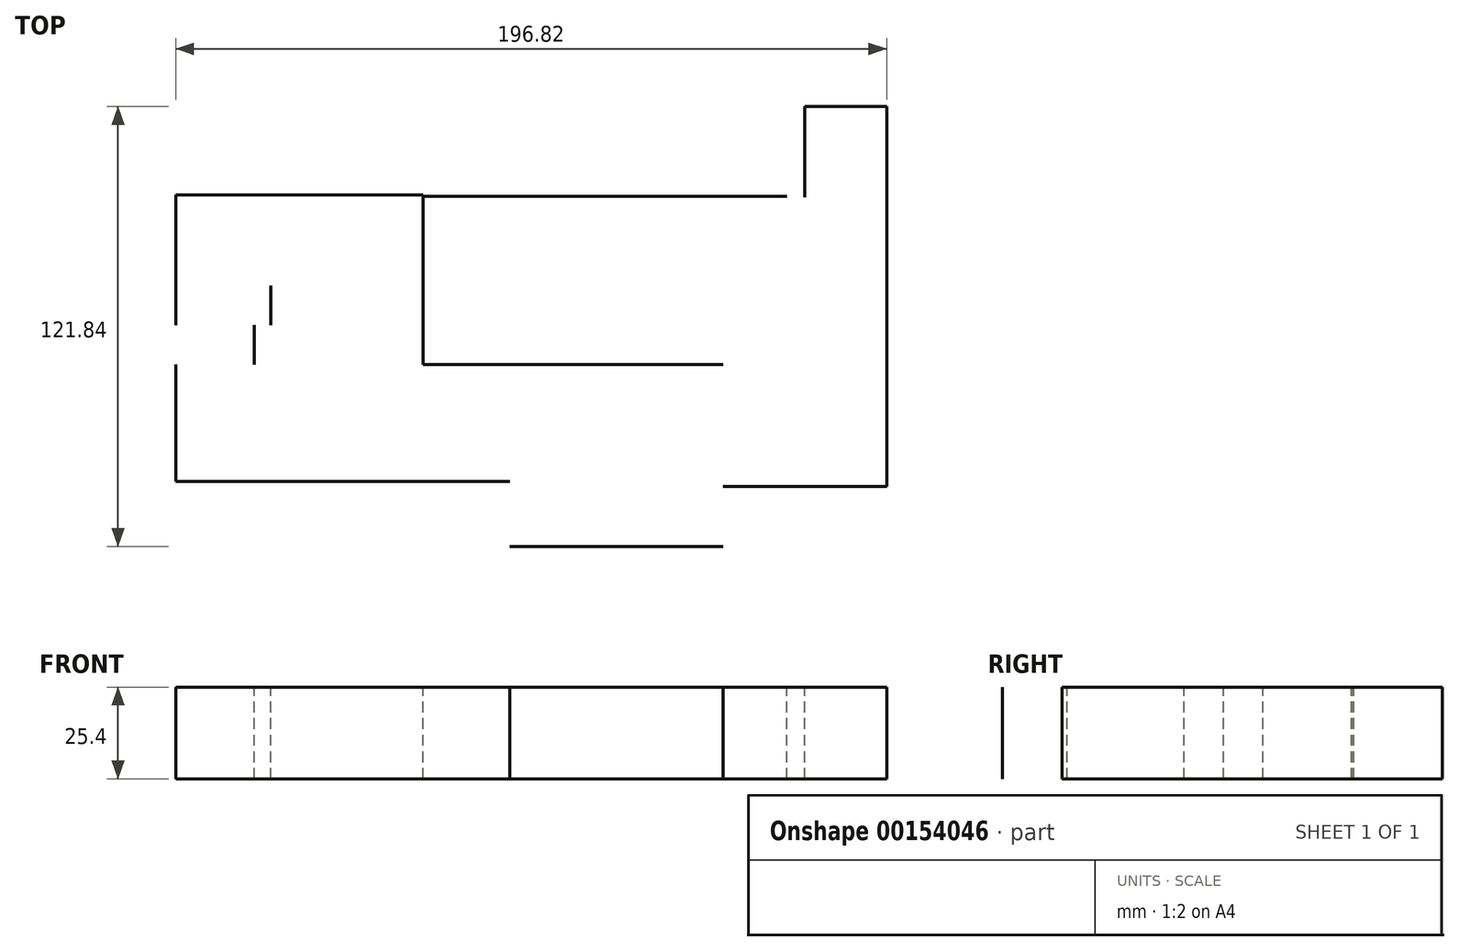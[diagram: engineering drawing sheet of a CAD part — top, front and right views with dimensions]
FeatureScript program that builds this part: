
annotation { "Feature Type Name" : "Feature", "Feature Type Description" : "" }
export const myFeature = defineFeature(function(context is Context, id is Id, definition is map)
    precondition{}
    {
        {
            var Q0;
            Q0=qCreatedBy(makeId("Top.planeOp"),FACE);
            var sketch = newSketch(context, id + "F0", { "sketchPlane" : qUnion([Q0])});
            skLineSegment(sketch, "E0.bottom", {"start": v(0, 0) * mm, "end": v(59.04, 0) * mm});
            skLineSegment(sketch, "E0.top", {"start": v(0, -50.34) * mm, "end": v(59.04, -50.34) * mm});
            skLineSegment(sketch, "E0.left", {"start": v(0, 0) * mm, "end": v(0, -50.34) * mm});
            skLineSegment(sketch, "E0.right", {"start": v(59.04, 0) * mm, "end": v(59.04, -50.34) * mm});
            skLineSegment(sketch, "E1.bottom", {"start": v(59.04, -33.8) * mm, "end": v(104.4, -33.8) * mm});
            skLineSegment(sketch, "E1.top", {"start": v(59.04, 46.35) * mm, "end": v(104.4, 46.35) * mm});
            skLineSegment(sketch, "E1.left", {"start": v(59.04, -33.8) * mm, "end": v(59.04, 46.35) * mm});
            skLineSegment(sketch, "E1.right", {"start": v(104.4, -33.8) * mm, "end": v(104.4, 46.35) * mm});
            skLineSegment(sketch, "E2.bottom", {"start": v(59.04, 0) * mm, "end": v(-23.96, 0) * mm});
            skLineSegment(sketch, "E2.top", {"start": v(59.04, 46.64) * mm, "end": v(-23.96, 46.64) * mm});
            skLineSegment(sketch, "E2.left", {"start": v(59.04, 0) * mm, "end": v(59.04, 46.64) * mm});
            skLineSegment(sketch, "E2.right", {"start": v(-23.96, 0) * mm, "end": v(-23.96, 46.64) * mm});
            skLineSegment(sketch, "E3.bottom", {"start": v(0, 0) * mm, "end": v(-28.52, 0) * mm});
            skLineSegment(sketch, "E3.top", {"start": v(0, -32.37) * mm, "end": v(-28.52, -32.37) * mm});
            skLineSegment(sketch, "E3.left", {"start": v(0, 0) * mm, "end": v(0, -32.37) * mm});
            skLineSegment(sketch, "E4.bottom", {"start": v(-28.52, -32.37) * mm, "end": v(-92.42, -32.37) * mm});
            skLineSegment(sketch, "E4.right", {"start": v(-92.42, -32.37) * mm, "end": v(-92.42, 0) * mm});
            skLineSegment(sketch, "E5.top", {"start": v(-23.96, 0) * mm, "end": v(-28.52, 0) * mm});
            skLineSegment(sketch, "E5.left", {"start": v(-23.96, 46.64) * mm, "end": v(-23.96, 0) * mm});
            skLineSegment(sketch, "E6.bottom", {"start": v(-92.42, 0) * mm, "end": v(-70.74, 0) * mm});
            skLineSegment(sketch, "E7.bottom", {"start": v(59.04, 46.64) * mm, "end": v(76.73, 46.64) * mm});
            skLineSegment(sketch, "E7.top", {"start": v(59.04, 17.26) * mm, "end": v(76.73, 17.26) * mm});
            skLineSegment(sketch, "E7.left", {"start": v(59.04, 46.64) * mm, "end": v(59.04, 17.26) * mm});
            skLineSegment(sketch, "E7.right", {"start": v(76.73, 46.64) * mm, "end": v(76.73, 17.26) * mm});
            skLineSegment(sketch, "E8.bottom", {"start": v(0, -32.37) * mm, "end": v(-12.27, -32.37) * mm});
            skLineSegment(sketch, "E8.top", {"start": v(0, -20.4) * mm, "end": v(-12.27, -20.4) * mm});
            skLineSegment(sketch, "E8.left", {"start": v(0, -32.37) * mm, "end": v(0, -20.4) * mm});
            skLineSegment(sketch, "E8.right", {"start": v(-12.27, -32.37) * mm, "end": v(-12.27, -20.4) * mm});
            skLineSegment(sketch, "E9.bottom", {"start": v(0, 0) * mm, "end": v(-12.27, 0) * mm});
            skLineSegment(sketch, "E9.left", {"start": v(0, 0) * mm, "end": v(0, -20.4) * mm});
            skLineSegment(sketch, "E9.right", {"start": v(-12.27, 0) * mm, "end": v(-12.27, -20.4) * mm});
            skLineSegment(sketch, "E10.top", {"start": v(-92.42, -8.99) * mm, "end": v(-70.74, -8.99) * mm});
            skLineSegment(sketch, "E10.left", {"start": v(-92.42, 0) * mm, "end": v(-92.42, -8.99) * mm});
            skLineSegment(sketch, "E10.right", {"start": v(-70.74, 0) * mm, "end": v(-70.74, -8.99) * mm});
            skLineSegment(sketch, "E11.trimOffspring", {"start": v(-70.74, 0) * mm, "end": v(-92.42, 0) * mm});
            skLineSegment(sketch, "E12.bottom", {"start": v(-92.42, 0) * mm, "end": v(-23.96, 0) * mm});
            skLineSegment(sketch, "E12.top", {"start": v(-92.42, 10.95) * mm, "end": v(-23.96, 10.95) * mm});
            skLineSegment(sketch, "E12.left", {"start": v(-92.42, 0) * mm, "end": v(-92.42, 10.95) * mm});
            skLineSegment(sketch, "E12.right", {"start": v(-23.96, 0) * mm, "end": v(-23.96, 10.95) * mm});
            skLineSegment(sketch, "E13", {"start": v(-51.9, 0) * mm, "end": v(-51.9, -32.37) * mm});
            skLineSegment(sketch, "E14.bottom", {"start": v(-23.96, 10.95) * mm, "end": v(-51.58, 10.95) * mm});
            skLineSegment(sketch, "E14.top", {"start": v(-23.96, 47) * mm, "end": v(-51.58, 47) * mm});
            skLineSegment(sketch, "E14.left", {"start": v(-23.96, 10.95) * mm, "end": v(-23.96, 47) * mm});
            skLineSegment(sketch, "E14.right", {"start": v(-51.58, 10.95) * mm, "end": v(-51.58, 47) * mm});
            skLineSegment(sketch, "E15.bottom", {"start": v(-92.42, 10.95) * mm, "end": v(-51.58, 10.95) * mm});
            skLineSegment(sketch, "E15.top", {"start": v(-92.42, 47) * mm, "end": v(-51.58, 47) * mm});
            skLineSegment(sketch, "E15.left", {"start": v(-92.42, 10.95) * mm, "end": v(-92.42, 47) * mm});
            skLineSegment(sketch, "E16.bottom", {"start": v(-66.15, 10.95) * mm, "end": v(-92.42, 10.95) * mm});
            skLineSegment(sketch, "E16.top", {"start": v(-66.15, 21.87) * mm, "end": v(-92.42, 21.87) * mm});
            skLineSegment(sketch, "E16.left", {"start": v(-66.15, 10.95) * mm, "end": v(-66.15, 21.87) * mm});
            skLineSegment(sketch, "E16.right", {"start": v(-92.42, 10.95) * mm, "end": v(-92.42, 21.87) * mm});
            skLineSegment(sketch, "E17", {"start": v(-70.74, 0) * mm, "end": v(-70.74, 10.95) * mm});
            skLineSegment(sketch, "E18.bottom", {"start": v(104.4, 46.35) * mm, "end": v(81.65, 46.35) * mm});
            skLineSegment(sketch, "E18.top", {"start": v(104.4, 71.5) * mm, "end": v(81.65, 71.5) * mm});
            skLineSegment(sketch, "E18.left", {"start": v(104.4, 46.35) * mm, "end": v(104.4, 71.5) * mm});
            skLineSegment(sketch, "E18.right", {"start": v(81.65, 46.35) * mm, "end": v(81.65, 71.5) * mm});
            skSolve(sketch);
        }
        {
            var Q0;
            Q0=sQuery(id+"F0.wireOp",EDGE,"E15.top");
            var Q1;
            Q1=sQuery(id+"F0.wireOp",EDGE,"E15.left");
            var Q2;
            Q2=sQuery(id+"F0.wireOp",EDGE,"E14.top");
            var Q3;
            Q3=sQuery(id+"F0.wireOp",EDGE,"E2.top");
            var Q4;
            Q4=sQuery(id+"F0.wireOp",EDGE,"E7.bottom");
            var Q5;
            Q5=sQuery(id+"F0.wireOp",EDGE,"E18.right");
            var Q6;
            Q6=sQuery(id+"F0.wireOp",EDGE,"E18.top");
            var Q7;
            Q7=sQuery(id+"F0.wireOp",EDGE,"E18.left");
            var Q8;
            Q8=sQuery(id+"F0.wireOp",EDGE,"E1.right");
            var Q9;
            Q9=sQuery(id+"F0.wireOp",EDGE,"E1.bottom");
            var Q10;
            Q10=sQuery(id+"F0.wireOp",EDGE,"E0.top");
            var Q11;
            Q11=sQuery(id+"F0.wireOp",EDGE,"E4.right");
            var Q12;
            Q12=sQuery(id+"F0.wireOp",EDGE,"E4.bottom");
            var Q13;
            Q13=sQuery(id+"F0.wireOp",EDGE,"E3.top");
            var Q14;
            Q14=sQuery(id+"F0.wireOp",EDGE,"E2.bottom");
            var Q15;
            Q15=sQuery(id+"F0.wireOp",EDGE,"E5.left");
            var Q16;
            Q16=sQuery(id+"F0.wireOp",EDGE,"E17");
            var Q17;
            Q17=sQuery(id+"F0.wireOp",EDGE,"E16.left");
            extrude(context, id + "F1", {"bodyType" : ToolBodyType.SURFACE, "surfaceEntities" : qUnion([Q0, Q1, Q2, Q3, Q4, Q5, Q6, Q7, Q8, Q9, Q10, Q11, Q12, Q13, Q14, Q15, Q16, Q17]), "depth" : 25.4 * mm});
        }
    });
